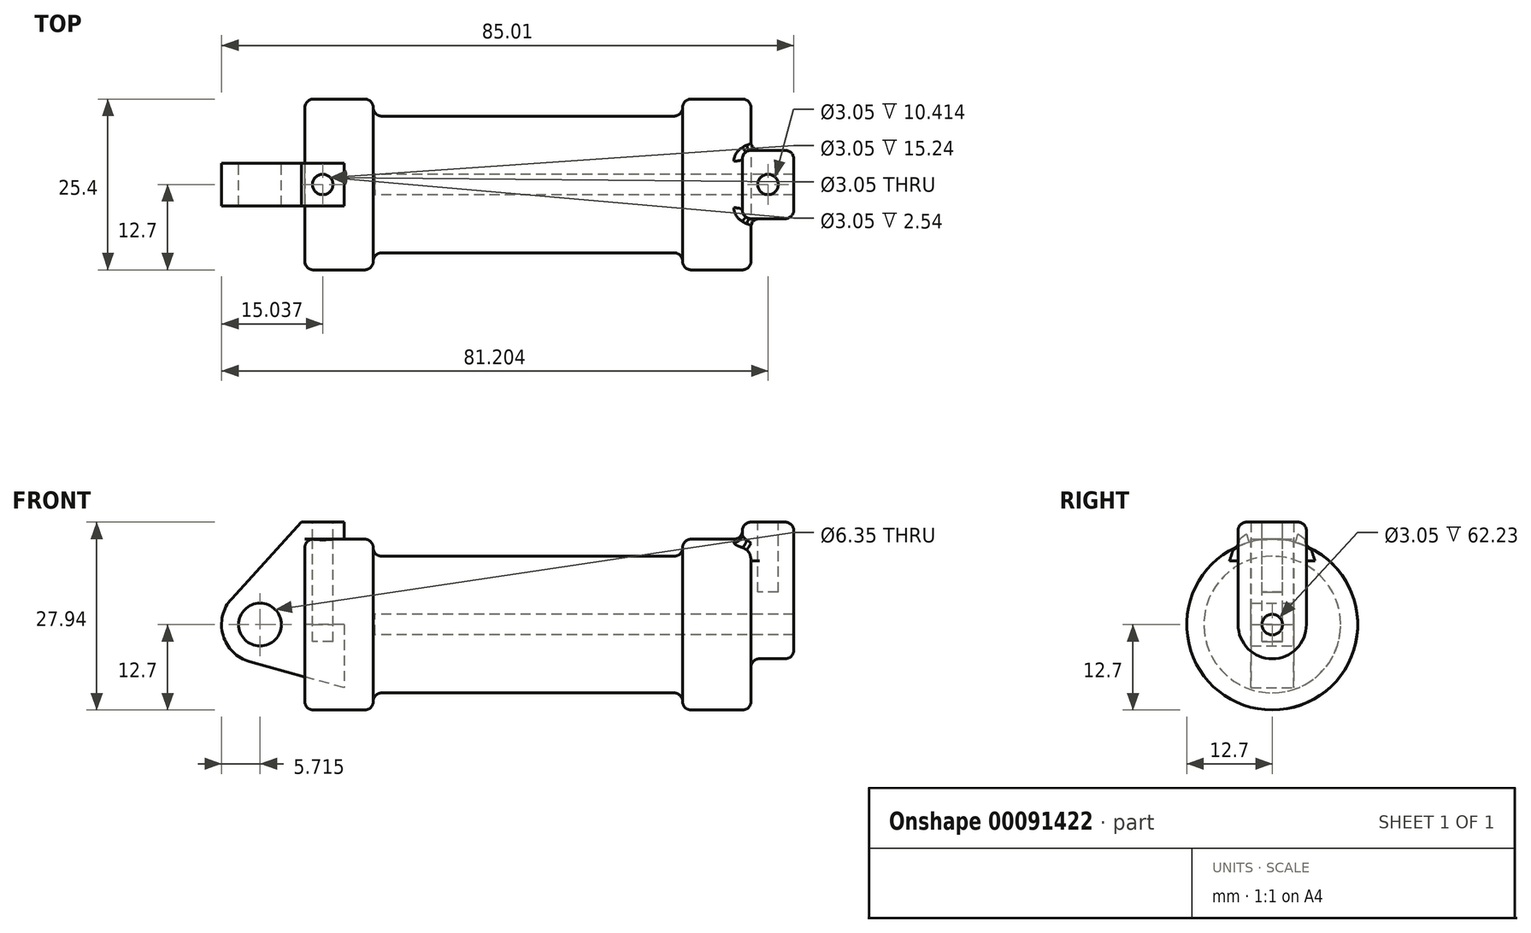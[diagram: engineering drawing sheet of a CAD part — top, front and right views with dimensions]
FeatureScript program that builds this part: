
annotation { "Feature Type Name" : "Feature", "Feature Type Description" : "" }
export const myFeature = defineFeature(function(context is Context, id is Id, definition is map)
    precondition{}
    {
        {
            var Q0;
            Q0=qCreatedBy(makeId("Front.planeOp"),FACE);
            var sketch = newSketch(context, id + "F0", { "sketchPlane" : qUnion([Q0])});
            skLineSegment(sketch, "E0", {"start": v(0, 0) * mm, "end": v(0, 12.7) * mm});
            skLineSegment(sketch, "E1", {"start": v(0, 12.7) * mm, "end": v(10.16, 12.7) * mm});
            skLineSegment(sketch, "E2", {"start": v(10.16, 12.7) * mm, "end": v(10.16, 10.16) * mm});
            skLineSegment(sketch, "E3", {"start": v(10.16, 10.16) * mm, "end": v(56.13, 10.16) * mm});
            skLineSegment(sketch, "E4", {"start": v(56.13, 10.16) * mm, "end": v(56.13, 12.7) * mm});
            skLineSegment(sketch, "E5", {"start": v(56.13, 12.7) * mm, "end": v(66.3, 12.7) * mm});
            skLineSegment(sketch, "E6", {"start": v(66.3, 12.7) * mm, "end": v(66.3, 0) * mm});
            skLineSegment(sketch, "E7", {"start": v(66.3, 0) * mm, "end": v(0, 0) * mm});
            skLineSegment(sketch, "E8", {"start": v(5.84, 15.24) * mm, "end": v(-0.5, 15.24) * mm});
            skLineSegment(sketch, "E9", {"start": v(-0.5, 15.24) * mm, "end": v(-10.88, 3.85) * mm});
            skLineSegment(sketch, "E10", {"start": v(0, 0) * mm, "end": v(-6.65, 0) * mm});
            skCircle(sketch, "E11", {"center": v(-6.65, 0) * mm, "radius": 5.72 * mm});
            skCircle(sketch, "E12", {"center": v(-6.65, 0) * mm, "radius": 3.18 * mm});
            skLineSegment(sketch, "E13", {"start": v(5.84, 15.24) * mm, "end": v(5.84, -9.4) * mm});
            skLineSegment(sketch, "E14", {"start": v(5.84, -9.4) * mm, "end": v(-8.18, -5.5) * mm});
            skSolve(sketch);
        }
        {
            var Q0;
            {var subQ3=sQuery(id+"F0.wireOp",EDGE,"E0");Q0=makeQuery(id+"F0.imprint","IMPRINT",FACE,{"disambiguationData":[TD([[makeQuery(id+"F0.imprint","IMPRINT",EDGE,{"derivedFrom":subQ3}),1.0]])]});}
            var Q1;
            {var subQ4=sQuery(id+"F0.wireOp",EDGE,"E12");Q1=makeQuery(id+"F0.imprint","IMPRINT",FACE,{"disambiguationData":[TD([[makeQuery(id+"F0.imprint","IMPRINT",EDGE,{"derivedFrom":subQ4}),-1.0]])]});}
            var Q2;
            {var subQ0=sQuery(id+"F0.wireOp",EDGE,"E14");Q2=makeQuery(id+"F0.imprint","IMPRINT",FACE,{"disambiguationData":[TD([[makeQuery(id+"F0.imprint","IMPRINT",EDGE,{"derivedFrom":subQ0}),-1.0]])]});}
            extrude(context, id + "F1", {"entities" : qUnion([Q0, Q1, Q2]), "depth" : 3.17 * mm, "hasSecondDirection" : true, "secondDirectionOppositeDirection" : true, "secondDirectionDepth" : 3.17 * mm});
        }
        {
            var Q0;
            {var subQ0=sQuery(id+"F0.wireOp",EDGE,"E2");Q0=makeQuery(id+"F0.imprint","IMPRINT",FACE,{"disambiguationData":[TD([[makeQuery(id+"F0.imprint","IMPRINT",EDGE,{"derivedFrom":subQ0}),-1.0]])]});}
            var Q1;
            {var subQ0=sQuery(id+"F0.wireOp",EDGE,"E0");Q1=makeQuery(id+"F0.imprint","IMPRINT",FACE,{"disambiguationData":[TD([[makeQuery(id+"F0.imprint","IMPRINT",EDGE,{"derivedFrom":subQ0}),-1.0]])]});}
            var Q2;
            Q2=sQuery(id+"F0.wireOp",EDGE,"E7");
            revolve(context, id + "F2", {"entities" : qUnion([Q0, Q1]), "axis" : qUnion([Q2]), "revolveType" : RevolveType.FULL});
        }
        {
            var Q0;
            Q0=makeQuery(id+"F2.opRevolve","SWEPT_FACE",FACE,{"disambiguationData":[OSD([sQuery(id+"F0.wireOp",EDGE,"E6")])]});
            var sketch = newSketch(context, id + "F3", { "sketchPlane" : qUnion([Q0])});
            skCircle(sketch, "E15", {"center": v(0, 0) * mm, "radius": 1.52 * mm});
            skCircle(sketch, "E16", {"center": v(0, 0) * mm, "radius": 5.08 * mm});
            skLineSegment(sketch, "E17", {"start": v(-5.08, 0) * mm, "end": v(-5.08, 15.24) * mm});
            skLineSegment(sketch, "E18", {"start": v(-5.08, 15.24) * mm, "end": v(5.08, 15.24) * mm});
            skLineSegment(sketch, "E19", {"start": v(5.08, 15.24) * mm, "end": v(5.08, 0) * mm});
            skSolve(sketch);
        }
        {
            var Q0;
            {var subQ0=sQuery(id+"F3.wireOp",EDGE,"E18");Q0=makeQuery(id+"F3.imprint","IMPRINT",FACE,{"disambiguationData":[TD([[makeQuery(id+"F3.imprint","IMPRINT",EDGE,{"derivedFrom":subQ0}),-1.0]])]});}
            var Q1;
            {var subQ0=sQuery(id+"F3.wireOp",EDGE,"E17");var subQ1=sQuery(id+"F3.wireOp",EDGE,"E16");var subQ2=makeQuery(id+"F3.imprint","INTERSECT",VERTEX,{"derivedFrom":[subQ1,subQ0]});Q1=makeQuery(id+"F3.imprint","IMPRINT",FACE,{"disambiguationData":[TD([[makeQuery(id+"F3.imprint","IMPRINT",EDGE,{"disambiguationData":[TD([[subQ2,1.0]])],"derivedFrom":subQ1}),-1.0]])]});}
            var Q2;
            Q2=makeQuery(id+"F3.imprint","IMPRINT",FACE,{"disambiguationData":[TD([[makeQuery(id+"F3.imprint","IMPRINT",EDGE,{"derivedFrom":sQuery(id+"F3.wireOp",EDGE,"E15")}),-1.0]])]});
            extrude(context, id + "F4", {"entities" : qUnion([Q0, Q1, Q2]), "operationType" : NewBodyOperationType.ADD, "depth" : 6.35 * mm, "hasSecondDirection" : true, "secondDirectionOppositeDirection" : true, "secondDirectionDepth" : 1.27 * mm});
        }
        {
            var Q0;
            Q0=makeQuery(id+"F3.imprint","IMPRINT",FACE,{"disambiguationData":[TD([[makeQuery(id+"F3.imprint","IMPRINT",EDGE,{"derivedFrom":sQuery(id+"F3.wireOp",EDGE,"E15")}),1.0]])]});
            extrude(context, id + "F5", {"entities" : qUnion([Q0]), "operationType" : NewBodyOperationType.REMOVE, "oppositeDirection" : true, "depth" : 55.88 * mm});
        }
        {
            var Q0;
            Q0=makeQuery(id+"F4.opExtrude","SWEPT_FACE",FACE,{"disambiguationData":[OSD([sQuery(id+"F3.wireOp",EDGE,"E18")])]});
            var sketch = newSketch(context, id + "F6", { "sketchPlane" : qUnion([Q0])});
            skLineSegment(sketch, "E20", {"start": v(65.02, 0) * mm, "end": v(72.64, 0) * mm, "construction": true});
            skCircle(sketch, "E21", {"center": v(68.83, 0) * mm, "radius": 1.52 * mm});
            skSolve(sketch);
        }
        {
            var Q0;
            Q0=makeQuery(id+"F6.imprint","IMPRINT",FACE,{"disambiguationData":[TD([[makeQuery(id+"F6.imprint","IMPRINT",EDGE,{"derivedFrom":sQuery(id+"F6.wireOp",EDGE,"E21")}),1.0]])]});
            extrude(context, id + "F7", {"entities" : qUnion([Q0]), "operationType" : NewBodyOperationType.REMOVE, "oppositeDirection" : true, "depth" : 10.4 * mm});
        }
        {
            var Q0;
            Q0=makeQuery(id+"F1.opExtrude","SWEPT_FACE",FACE,{"disambiguationData":[OSD([sQuery(id+"F0.wireOp",EDGE,"E8")])]});
            var sketch = newSketch(context, id + "F8", { "sketchPlane" : qUnion([Q0])});
            skLineSegment(sketch, "E22", {"start": v(-0.5, 0) * mm, "end": v(5.84, 0) * mm, "construction": true});
            skCircle(sketch, "E23", {"center": v(2.67, 0) * mm, "radius": 1.52 * mm});
            skSolve(sketch);
        }
        {
            var Q0;
            Q0=makeQuery(id+"F8.imprint","IMPRINT",FACE,{"disambiguationData":[TD([[makeQuery(id+"F8.imprint","IMPRINT",EDGE,{"derivedFrom":sQuery(id+"F8.wireOp",EDGE,"E23")}),1.0]])]});
            extrude(context, id + "F9", {"entities" : qUnion([Q0]), "operationType" : NewBodyOperationType.REMOVE, "oppositeDirection" : true, "depth" : 17.78 * mm});
        }
        {
            var Q0;
            Q0=makeQuery(id+"F2.opRevolve","SWEPT_EDGE",EDGE,{"disambiguationData":[OSD([sQuery(id+"F0.wireOp",EDGE,"E1"),sQuery(id+"F0.wireOp",EDGE,"E2")])]});
            var Q1;
            Q1=makeQuery(id+"F2.opRevolve","SWEPT_EDGE",EDGE,{"disambiguationData":[OSD([sQuery(id+"F0.wireOp",EDGE,"E0"),sQuery(id+"F0.wireOp",EDGE,"E1")])]});
            var Q2;
            Q2=makeQuery(id+"F2.opRevolve","SWEPT_EDGE",EDGE,{"disambiguationData":[OSD([sQuery(id+"F0.wireOp",EDGE,"E5"),sQuery(id+"F0.wireOp",EDGE,"E6")])]});
            var Q3;
            Q3=makeQuery(id+"F2.opRevolve","SWEPT_EDGE",EDGE,{"disambiguationData":[OSD([sQuery(id+"F0.wireOp",EDGE,"E4"),sQuery(id+"F0.wireOp",EDGE,"E5")])]});
            var Q4;
            Q4=makeQuery(id+"F2.opRevolve","SWEPT_EDGE",EDGE,{"disambiguationData":[OSD([sQuery(id+"F0.wireOp",EDGE,"E2"),sQuery(id+"F0.wireOp",EDGE,"E3")])]});
            var Q5;
            Q5=makeQuery(id+"F2.opRevolve","SWEPT_EDGE",EDGE,{"disambiguationData":[OSD([sQuery(id+"F0.wireOp",EDGE,"E3"),sQuery(id+"F0.wireOp",EDGE,"E4")])]});
            fillet(context, id + "F10", {"entities" : qUnion([Q0, Q1, Q2, Q3, Q4, Q5]), "radius" : 1.27 * mm, "tangentPropagation" : true, "allowEdgeOverflow" : false});
        }
        {
            var Q0;
            Q0=makeQuery(id+"F4.opExtrude","SWEPT_EDGE",EDGE,{"disambiguationData":[OSD([sQuery(id+"F3.wireOp",EDGE,"E17"),sQuery(id+"F3.wireOp",EDGE,"E18")])]});
            var Q1;
            Q1=makeQuery(id+"F4.opExtrude","CAP_EDGE",EDGE,{"disambiguationData":[OSD([sQuery(id+"F3.wireOp",EDGE,"E17")])],"isStart":true});
            var Q2;
            Q2=makeQuery(id+"F10.opFillet","BLEND_EDGE",EDGE,{"blendedFrom":[makeQuery(id+"F2.opRevolve","SWEPT_EDGE",EDGE,{"disambiguationData":[OSD([sQuery(id+"F0.wireOp",EDGE,"E5"),sQuery(id+"F0.wireOp",EDGE,"E6")])]}),makeQuery(id+"F4.opExtrude","SWEPT_FACE",FACE,{"disambiguationData":[OSD([sQuery(id+"F3.wireOp",EDGE,"E17")])]})],"blendedInto":[makeQuery(id+"F4.opExtrude","SWEPT_FACE",FACE,{"disambiguationData":[OSD([sQuery(id+"F3.wireOp",EDGE,"E17")])]})]});
            var Q3;
            Q3=makeQuery(id+"F4.opExtrude","CAP_EDGE",EDGE,{"disambiguationData":[OSD([sQuery(id+"F3.wireOp",EDGE,"E16")])],"isStart":false});
            var Q4;
            Q4=makeQuery(id+"F4.opExtrude","CAP_EDGE",EDGE,{"disambiguationData":[OSD([sQuery(id+"F3.wireOp",EDGE,"E17")])],"isStart":false});
            var Q5;
            Q5=makeQuery(id+"F4.opExtrude","CAP_EDGE",EDGE,{"disambiguationData":[OSD([sQuery(id+"F3.wireOp",EDGE,"E19")])],"isStart":false});
            var Q6;
            Q6=makeQuery(id+"F4.opExtrude","CAP_EDGE",EDGE,{"disambiguationData":[OSD([sQuery(id+"F3.wireOp",EDGE,"E18")])],"isStart":false});
            var Q7;
            Q7=makeQuery(id+"F4.opExtrude","SWEPT_EDGE",EDGE,{"disambiguationData":[OSD([sQuery(id+"F3.wireOp",EDGE,"E18"),sQuery(id+"F3.wireOp",EDGE,"E19")])]});
            var Q8;
            Q8=makeQuery(id+"F10.opFillet","BLEND_EDGE",EDGE,{"blendedFrom":[makeQuery(id+"F2.opRevolve","SWEPT_EDGE",EDGE,{"disambiguationData":[OSD([sQuery(id+"F0.wireOp",EDGE,"E5"),sQuery(id+"F0.wireOp",EDGE,"E6")])]}),makeQuery(id+"F4.opExtrude","SWEPT_FACE",FACE,{"disambiguationData":[OSD([sQuery(id+"F3.wireOp",EDGE,"E19")])]})],"blendedInto":[makeQuery(id+"F4.opExtrude","SWEPT_FACE",FACE,{"disambiguationData":[OSD([sQuery(id+"F3.wireOp",EDGE,"E19")])]})]});
            var Q9;
            Q9=makeQuery(id+"F4.opExtrude","CAP_EDGE",EDGE,{"disambiguationData":[OSD([sQuery(id+"F3.wireOp",EDGE,"E19")])],"isStart":true});
            var Q10;
            Q10=makeQuery(id+"F4.boolean.opBoolean","INTERSECT",EDGE,{"derivedFrom":[makeQuery(id+"F2.opRevolve","SWEPT_FACE",FACE,{"disambiguationData":[OSD([sQuery(id+"F0.wireOp",EDGE,"E5")])]}),makeQuery(id+"F4.opExtrude","CAP_FACE",FACE,{"disambiguationData":[OSD([sQuery(id+"F3.wireOp",EDGE,"E15"),sQuery(id+"F3.wireOp",EDGE,"E16"),sQuery(id+"F3.wireOp",EDGE,"E17"),sQuery(id+"F3.wireOp",EDGE,"E18"),sQuery(id+"F3.wireOp",EDGE,"E19")])],"isStart":true})]});
            var Q11;
            Q11=makeQuery(id+"F4.opExtrude","CAP_EDGE",EDGE,{"disambiguationData":[OSD([sQuery(id+"F3.wireOp",EDGE,"E18")])],"isStart":true});
            fillet(context, id + "F11", {"entities" : qUnion([Q0, Q1, Q2, Q3, Q4, Q5, Q6, Q7, Q8, Q9, Q10, Q11]), "radius" : 1.27 * mm, "tangentPropagation" : true, "allowEdgeOverflow" : false});
        }
    });
